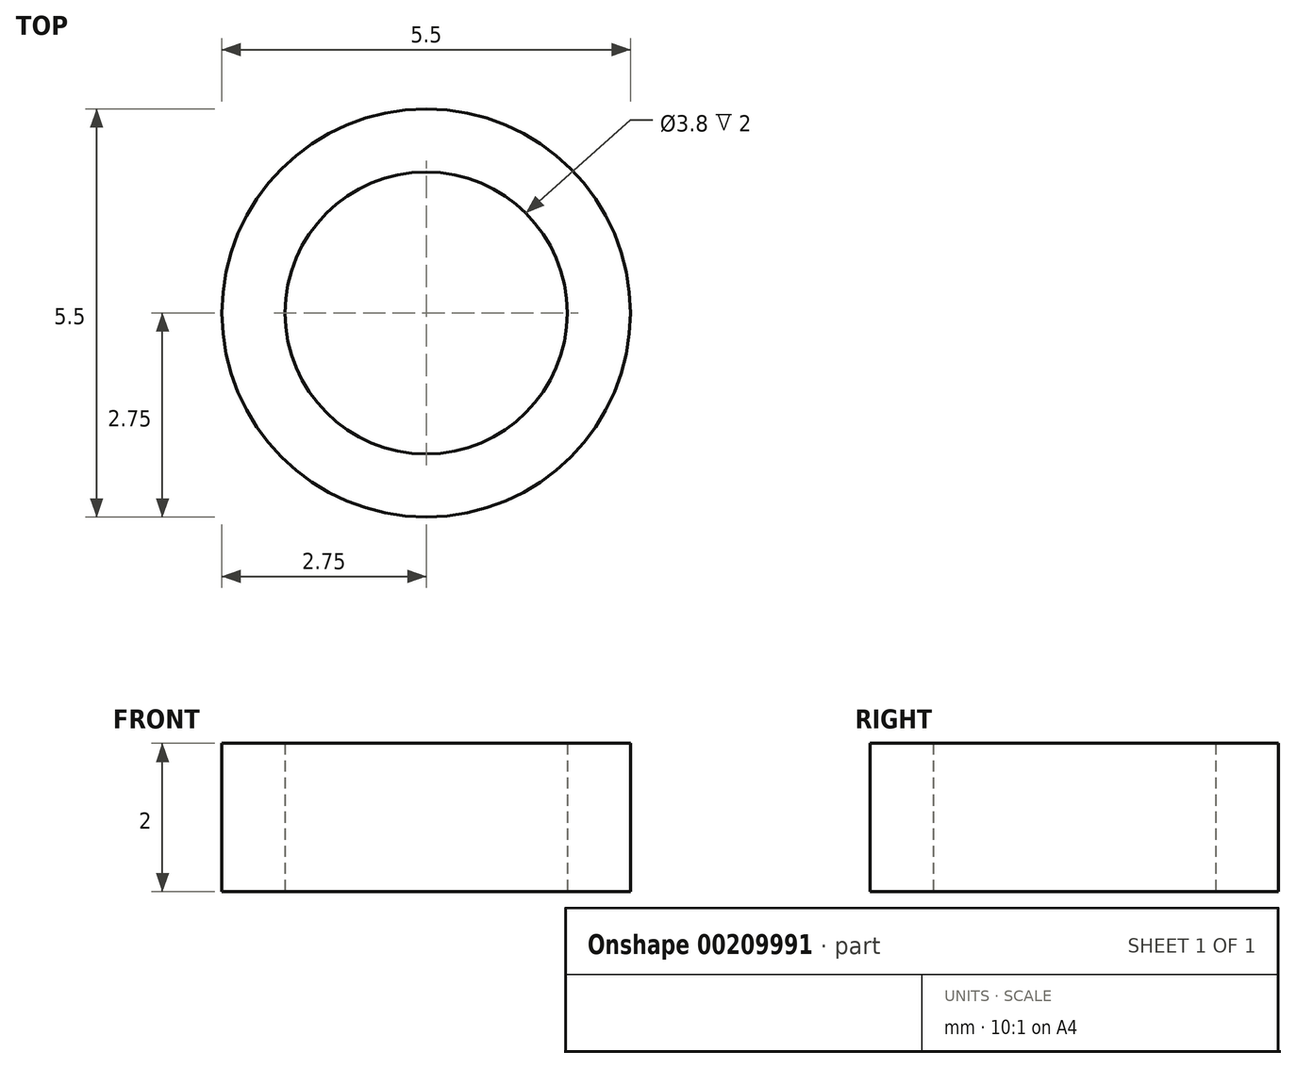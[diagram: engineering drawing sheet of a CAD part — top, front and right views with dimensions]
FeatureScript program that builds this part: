
annotation { "Feature Type Name" : "Feature", "Feature Type Description" : "" }
export const myFeature = defineFeature(function(context is Context, id is Id, definition is map)
    precondition{}
    {
        {
            var Q0;
            Q0=qCreatedBy(makeId("Top.planeOp"),FACE);
            var sketch = newSketch(context, id + "F0", { "sketchPlane" : qUnion([Q0])});
            skCircle(sketch, "E0", {"center": v(0, 0) * mm, "radius": 2.75 * mm});
            skCircle(sketch, "E1", {"center": v(0, 0) * mm, "radius": 1.9 * mm});
            skSolve(sketch);
        }
        {
            var Q0;
            Q0 = qSketchRegion(id + "F0", true);
            extrude(context, id + "F1", {"entities" : qUnion([Q0]), "depth" : 2 * mm, "offsetDistance" : 25 * mm});
        }
    });
